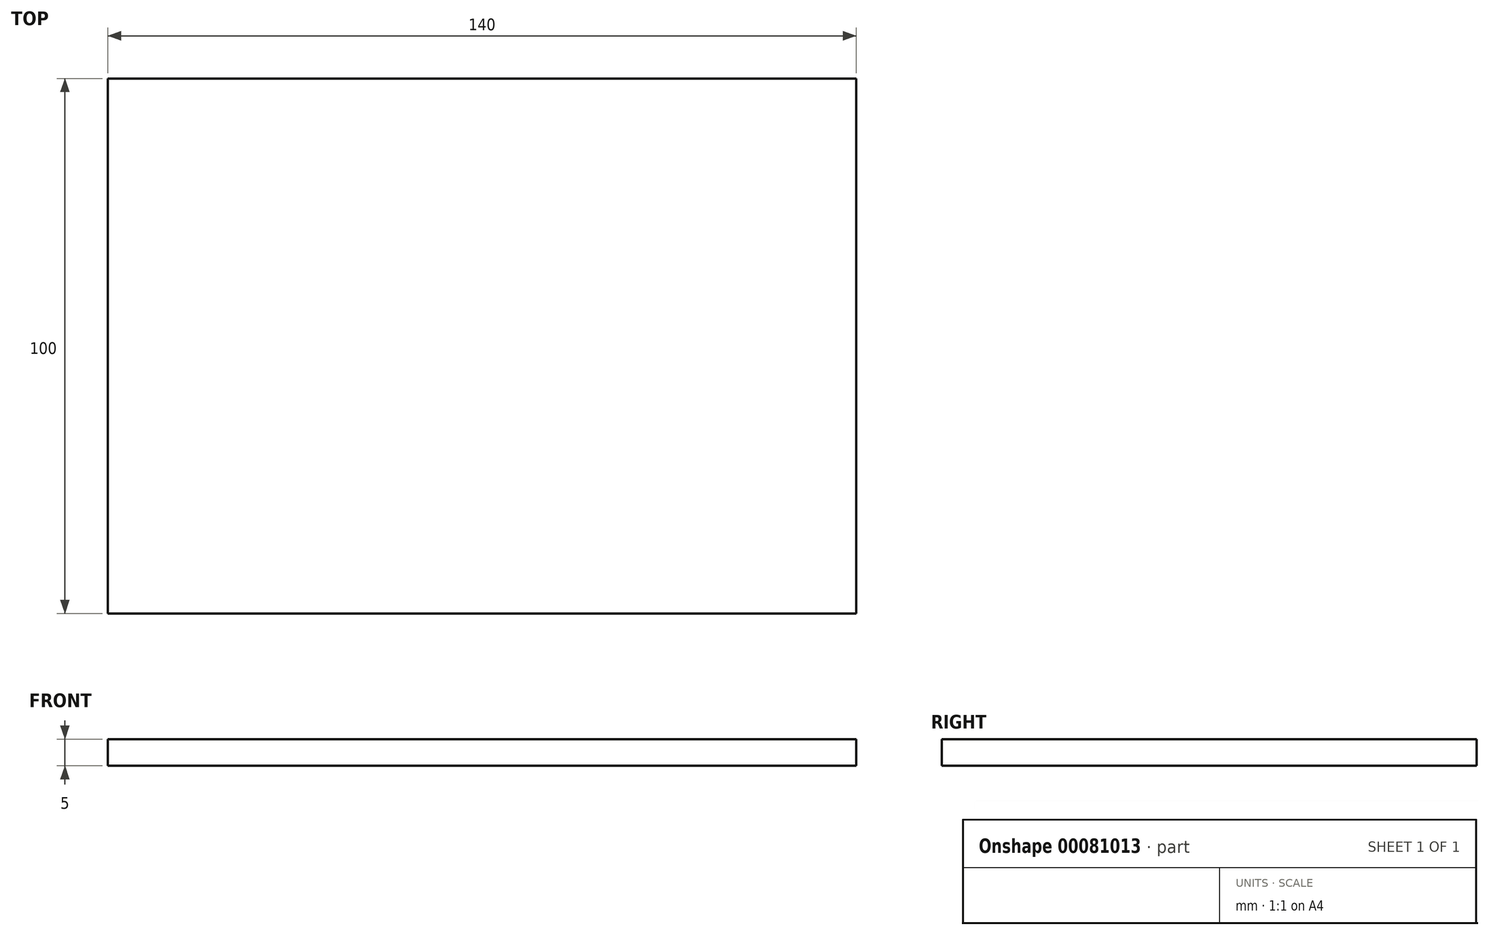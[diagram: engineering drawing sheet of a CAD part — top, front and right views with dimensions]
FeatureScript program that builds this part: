
annotation { "Feature Type Name" : "Feature", "Feature Type Description" : "" }
export const myFeature = defineFeature(function(context is Context, id is Id, definition is map)
    precondition{}
    {
        {
            var Q0;
            Q0=qCreatedBy(makeId("Top.planeOp"),FACE);
            var sketch = newSketch(context, id + "F0", { "sketchPlane" : qUnion([Q0])});
            skLineSegment(sketch, "E0.bottom", {"start": v(-140, -100) * mm, "end": v(0, -100) * mm});
            skLineSegment(sketch, "E0.top", {"start": v(-140, 0) * mm, "end": v(0, 0) * mm});
            skLineSegment(sketch, "E0.left", {"start": v(-140, -100) * mm, "end": v(-140, 0) * mm});
            skLineSegment(sketch, "E0.right", {"start": v(0, -100) * mm, "end": v(0, 0) * mm});
            skSolve(sketch);
        }
        {
            var Q0;
            Q0 = qSketchRegion(id + "F0", true);
            extrude(context, id + "F1", {"entities" : qUnion([Q0]), "endBound" : BoundingType.SYMMETRIC, "depth" : 5 * mm});
        }
    });
